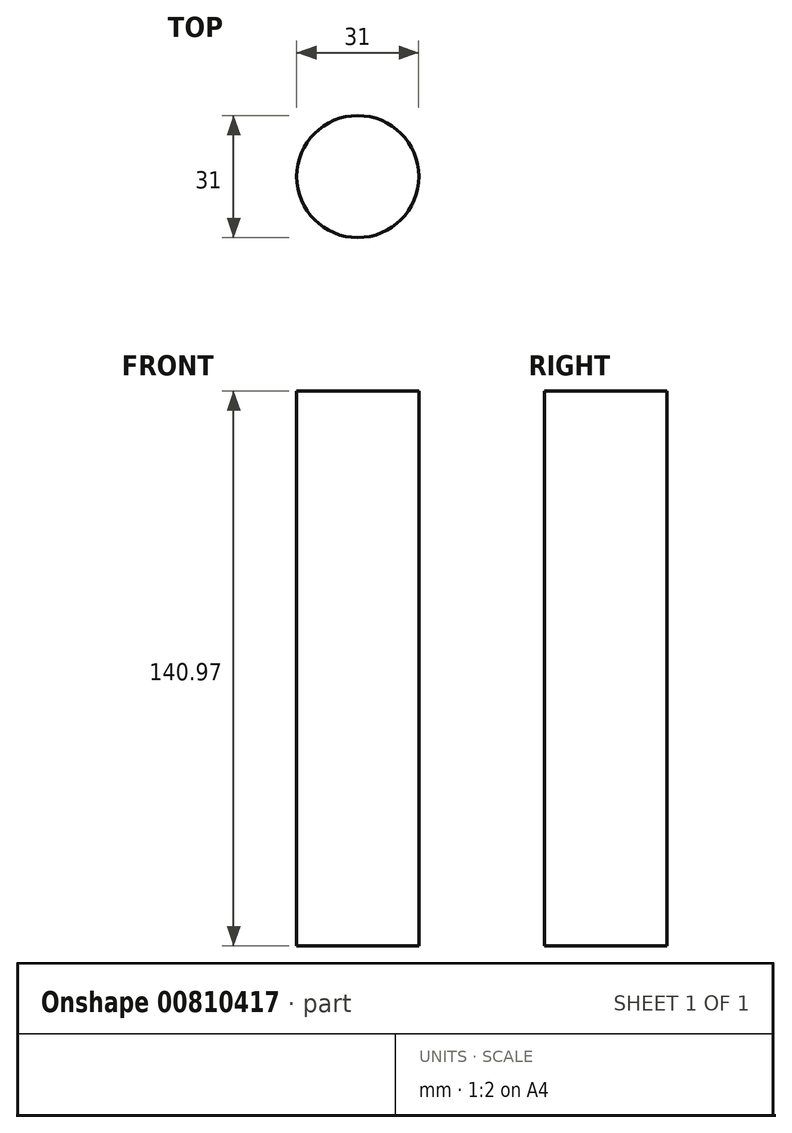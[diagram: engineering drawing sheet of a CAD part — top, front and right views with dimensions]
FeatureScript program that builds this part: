
annotation { "Feature Type Name" : "Feature", "Feature Type Description" : "" }
export const myFeature = defineFeature(function(context is Context, id is Id, definition is map)
    precondition{}
    {
        {
            var Q0;
            Q0=qCreatedBy(makeId("Top.planeOp"),FACE);
            var sketch = newSketch(context, id + "F0", { "sketchPlane" : qUnion([Q0])});
            skCircle(sketch, "E0", {"center": v(0, 44.47) * mm, "radius": 15.5 * mm});
            skSolve(sketch);
        }
        {
            var Q0;
            Q0=makeQuery(id+"F0.imprint","IMPRINT",FACE,{"disambiguationData":[TD([[makeQuery(id+"F0.imprint","IMPRINT",EDGE,{"derivedFrom":sQuery(id+"F0.wireOp",EDGE,"E0")}),1.0]])]});
            extrude(context, id + "F1", {"entities" : qUnion([Q0]), "oppositeDirection" : true, "depth" : 140.97 * mm, "offsetDistance" : 25.4 * mm});
        }
        {
            var Q0;
            Q0=qCreatedBy(makeId("Top.planeOp"),FACE);
            var sketch = newSketch(context, id + "F2", { "sketchPlane" : qUnion([Q0])});
            skCircle(sketch, "E1", {"center": v(-40.08, 9.9) * mm, "radius": 16.3 * mm});
            skSolve(sketch);
        }
        {
            var Q0;
            Q0=sQuery(id+"F2.wireOp",EDGE,"E1");
            extrude(context, id + "F3", {"bodyType" : ToolBodyType.SURFACE, "surfaceEntities" : qUnion([Q0]), "oppositeDirection" : true, "depth" : 135.64 * mm, "offsetDistance" : 25.4 * mm});
        }
    });
